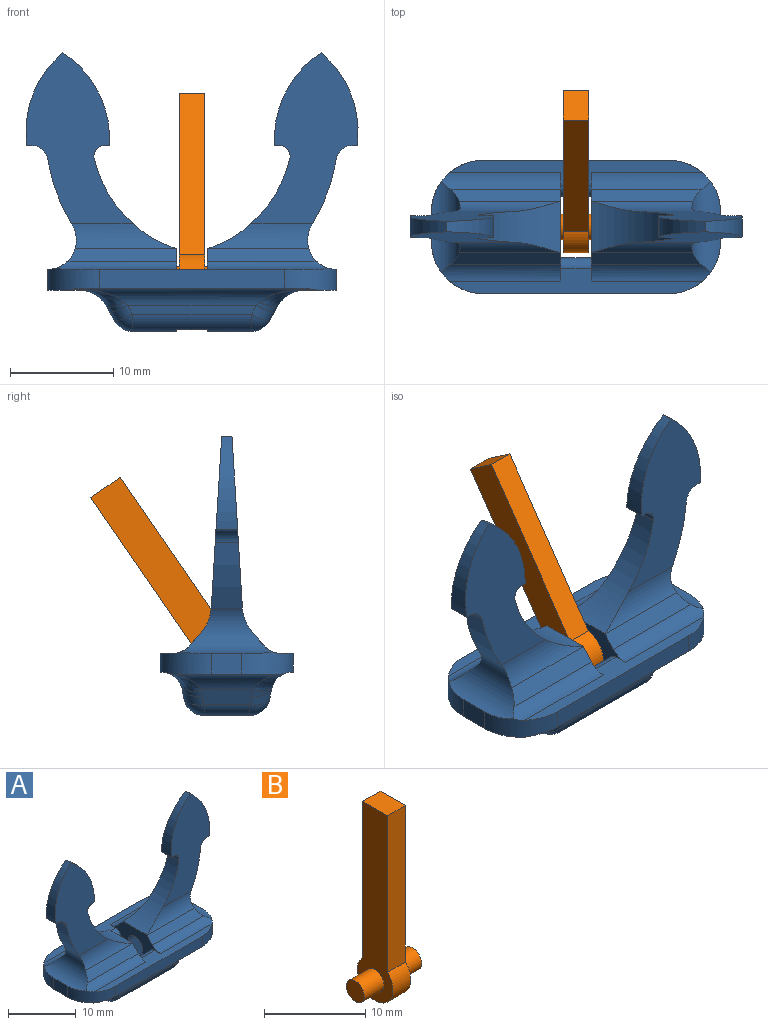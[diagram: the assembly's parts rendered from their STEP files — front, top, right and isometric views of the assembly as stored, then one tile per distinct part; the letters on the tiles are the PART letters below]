
ASSEMBLY  parts=2 mates=1
PART A: 96 faces, bbox 32.3x13x27.1 mm
  f0: plane 4.41x4.26mm, normal (0,0,-1), area 9.8mm2, adj f2,f10,f60,f61,f62,f75,f90
  f1: plane 10.48x8mm, normal (-1,0,0), area 31.6mm2, adj f3,f4,f24,f25,f35,f36,f50,f52
  f2: plane 10.48x8mm, normal (1,0,0), area 31.6mm2, adj f0,f4,f25,f26,f44,f45,f51,f53
  f3: plane 4.41x4.26mm, normal (0,0,-1), area 9.8mm2, adj f1,f11,f63,f64,f65,f75,f90
  f4: plane 24.54x2.46mm, normal (0,0,1), area 31.1mm2, adj f1,f2,f36,f38,f45,f68,f69,f82
  f5: cylinder r=2.8mm len=8.8mm, axis (0,1,0), area 33.5mm2, adj f6,f33,f43,f44,f45,f51,f53,f57
  f6: plane 2.91x2mm, normal (-1,0,0), area 5.8mm2, adj f5,f7,f66,f68
  f7: plane 10.31x3.07mm, normal (0,0,-1), area 28mm2, adj f6,f8,f66,f68,f80,f85
  f8: cylinder r=3mm len=10.31mm, axis (0,1,0), area 24.5mm2, adj f7,f9,f79,f86
  f9: plane 5.01x1.44mm, normal (-0.87,0,-0.49), area 7.7mm2, adj f8,f10,f77,f78,f87,f88
  f10: cylinder r=2mm len=4.41mm, axis (0,1,0), area 9.4mm2, adj f0,f9,f76,f89
  f11: cylinder r=2mm len=4.41mm, axis (0,1,0), area 9.4mm2, adj f3,f12,f74,f91
  f12: plane 5.01x1.44mm, normal (0.87,0,-0.49), area 7.7mm2, adj f11,f13,f72,f73,f92,f93
  f13: cylinder r=3mm len=10.31mm, axis (0,1,0), area 24.5mm2, adj f12,f14,f71,f94
  f14: plane 10.31x3.07mm, normal (0,0,-1), area 28mm2, adj f13,f15,f67,f69,f70,f95
  f15: plane 2.91x2mm, normal (1,0,0), area 5.8mm2, adj f14,f16,f67,f69
  f16: cylinder r=2.8mm len=8.8mm, axis (0,1,0), area 33.5mm2, adj f15,f17,f35,f36,f37,f50,f52,f56
  f17: cylinder r=18mm len=6.46mm, axis (0,1,0), area 18.3mm2, adj f16,f18,f34,f37,f54,f56
  f18: cylinder r=1.53mm len=2.25mm, axis (0,1,0), area 4.7mm2, adj f17,f19,f34,f54
  f19: plane 2.09x0.5mm, normal (0,0,-1), area 1mm2, adj f18,f20,f34,f54
  f20: cylinder r=10mm len=9mm, axis (0,1,0), area 15.6mm2, adj f19,f21,f34,f54
  f21: cylinder r=10mm len=9mm, axis (0,1,0), area 16.3mm2, adj f20,f22,f34,f54
  f22: plane 2.09x0.5mm, normal (0,0,-1), area 1mm2, adj f21,f23,f34,f54
  f23: cylinder r=1mm len=2.24mm, axis (0,1,0), area 3.9mm2, adj f22,f24,f34,f54
  f24: cylinder r=12mm len=8.78mm, axis (0,1,0), area 39.4mm2, adj f1,f23,f34,f37,f54,f56
  f25: plane 24.54x2.46mm, normal (0,0,1), area 31.1mm2, adj f1,f2,f49,f50,f51,f66,f67,f81
  f26: cylinder r=12mm len=8.78mm, axis (0,1,0), area 39.4mm2, adj f2,f27,f42,f43,f55,f57
  f27: cylinder r=1mm len=2.24mm, axis (0,1,0), area 3.9mm2, adj f26,f28,f42,f55
  f28: plane 2.09x0.5mm, normal (0,0,-1), area 1mm2, adj f27,f29,f42,f55
  f29: cylinder r=10mm len=9mm, axis (0,1,0), area 16.3mm2, adj f28,f30,f42,f55
  f30: cylinder r=10mm len=9mm, axis (0,1,0), area 15.6mm2, adj f29,f31,f42,f55
  f31: plane 2.09x0.5mm, normal (0,0,-1), area 1mm2, adj f30,f32,f42,f55
  f32: cylinder r=1.53mm len=2.25mm, axis (0,1,0), area 4.7mm2, adj f31,f33,f42,f55
  f33: cylinder r=18mm len=6.46mm, axis (0,1,0), area 18.3mm2, adj f5,f32,f42,f43,f55,f57
  f34: plane 16.68x10.47mm, normal (0,1,0.06), area 91.8mm2, adj f17,f18,f19,f20,f21,f22,f23,f24
  f35: plane 10.71x1.36mm, normal (0,0.75,0.66), area 17.1mm2, adj f1,f16,f36,f37
  f36: cylinder r=2.16mm len=11.54mm, axis (-1,0,0), area 20.4mm2, adj f1,f4,f16,f35,f69
  f37: cylinder r=4mm len=10.2mm, axis (-1,0,0), area 19.8mm2, adj f16,f17,f24,f34,f35
  f38: plane 18x1.83mm, normal (0,1,0), area 33mm2, adj f4,f39,f68,f69
  f39: plane 20.5x0.16mm, normal (0,0,-1), area 3.1mm2, adj f38,f40,f68,f69
  f40: cylinder r=2mm len=23.21mm, axis (-1,0,0), area 47.7mm2, adj f39,f41,f68,f69,f85,f86,f87,f93
  f41: plane 12.48x0.86mm, normal (0,0.98,-0.17), area 10.5mm2, adj f40,f88,f90,f92
  f42: plane 16.68x10.47mm, normal (0,1,0.06), area 91.8mm2, adj f26,f27,f28,f29,f30,f31,f32,f33
  f43: cylinder r=4mm len=10.2mm, axis (-1,0,0), area 19.8mm2, adj f5,f26,f33,f42,f44
  f44: plane 10.71x1.36mm, normal (0,0.75,0.66), area 17.1mm2, adj f2,f5,f43,f45
  f45: cylinder r=2.16mm len=11.54mm, axis (-1,0,0), area 20.4mm2, adj f2,f4,f5,f44,f68
  f46: plane 12.48x0.86mm, normal (0,-0.98,-0.17), area 10.5mm2, adj f48,f73,f75,f77
  f47: plane 20.5x0.16mm, normal (0,0,-1), area 3.1mm2, adj f48,f49,f66,f67
  f48: cylinder r=2mm len=23.21mm, axis (-1,0,0), area 47.7mm2, adj f46,f47,f66,f67,f70,f71,f72,f78
  f49: plane 18x1.83mm, normal (0,-1,0), area 33mm2, adj f25,f47,f66,f67
  f50: cylinder r=2.16mm len=11.54mm, axis (-1,0,0), area 20.4mm2, adj f1,f16,f25,f52,f67
  f51: cylinder r=2.16mm len=11.54mm, axis (-1,0,0), area 20.4mm2, adj f2,f5,f25,f53,f66
  f52: plane 10.71x1.36mm, normal (0,-0.75,0.66), area 17.1mm2, adj f1,f16,f50,f56
  f53: plane 10.71x1.36mm, normal (0,-0.75,0.66), area 17.1mm2, adj f2,f5,f51,f57
  f54: plane 16.68x10.47mm, normal (0,-1,0.06), area 91.8mm2, adj f17,f18,f19,f20,f21,f22,f23,f24
  f55: plane 16.68x10.47mm, normal (0,-1,0.06), area 91.8mm2, adj f26,f27,f28,f29,f30,f31,f32,f33
  f56: cylinder r=4mm len=10.2mm, axis (-1,0,0), area 19.8mm2, adj f16,f17,f24,f52,f54
  f57: cylinder r=4mm len=10.2mm, axis (-1,0,0), area 19.8mm2, adj f5,f26,f33,f53,f55
  f58: plane 4.84x3mm, normal (0,1,0), area 14.5mm2, adj f1,f2,f75,f81
  f59: plane 4.84x3mm, normal (0,-1,0), area 14.5mm2, adj f1,f2,f82,f90
  f60: plane 6.5x3mm, normal (1,0,0), area 18.5mm2, adj f0,f61,f62,f83
  f61: plane 5x3mm, normal (0,1,0), area 15mm2, adj f0,f2,f60,f83
  f62: plane 5x3mm, normal (0,-1,0), area 15mm2, adj f0,f2,f60,f83
  f63: plane 5x3mm, normal (0,-1,0), area 15mm2, adj f1,f3,f64,f84
  f64: plane 6.5x3mm, normal (-1,0,0), area 18.5mm2, adj f3,f63,f65,f84
  f65: plane 5x3mm, normal (0,1,0), area 15mm2, adj f1,f3,f64,f84
  f66: cylinder r=5mm len=5mm, axis (0,0,1), area 15.6mm2, adj f5,f6,f7,f25,f47,f48,f49,f51
  f67: cylinder r=5mm len=5mm, axis (0,0,-1), area 15.6mm2, adj f14,f15,f16,f25,f47,f48,f49,f50
  f68: cylinder r=5mm len=5mm, axis (0,0,-1), area 15.6mm2, adj f4,f5,f6,f7,f38,f39,f40,f45
  f69: cylinder r=5mm len=5mm, axis (0,0,1), area 15.6mm2, adj f4,f14,f15,f16,f36,f38,f39,f40
  f70: cylinder r=2mm len=1.44mm, axis (-1,0,0), area 0.6mm2, adj f14,f48,f67,f71
  f71: bspline ~4.69x3.31mm, area 6.7mm2, adj f13,f48,f70,f72
  f72: bspline ~2.07x2.04mm, area 1.5mm2, adj f12,f48,f71,f73
  f73: cylinder r=2mm len=2.23mm, axis (-0.48,0.15,-0.86), area 3mm2, adj f12,f46,f72,f74
  f74: sphere r=2mm, area 3.7mm2, adj f11,f73,f75
  f75: cylinder r=2mm len=11.52mm, axis (-1,0,0), area 29.7mm2, adj f0,f1,f2,f3,f46,f58,f74,f76
  f76: sphere r=2mm, area 3.7mm2, adj f10,f75,f77
  f77: cylinder r=2mm len=2.23mm, axis (-0.48,-0.15,0.86), area 3mm2, adj f9,f46,f76,f78
  f78: bspline ~2.07x2.04mm, area 1.5mm2, adj f9,f48,f77,f79
  f79: bspline ~5.07x3.39mm, area 6.7mm2, adj f8,f48,f78,f80
  f80: cylinder r=2mm len=1.44mm, axis (-1,0,0), area 0.6mm2, adj f7,f48,f66,f79
  f81: cylinder r=1mm len=3mm, axis (-1,0,0), area 4.7mm2, adj f1,f2,f25,f58
  f82: cylinder r=1mm len=3mm, axis (1,0,0), area 4.7mm2, adj f1,f2,f4,f59
  f83: cylinder r=1.5mm len=3mm, axis (1,0,0), area 14.1mm2, adj f2,f60,f61,f62
  f84: cylinder r=1.5mm len=3mm, axis (1,0,0), area 14.1mm2, adj f1,f63,f64,f65
  f85: cylinder r=2mm len=1.44mm, axis (-1,0,0), area 0.6mm2, adj f7,f40,f68,f86
  f86: bspline ~4.69x3.31mm, area 6.7mm2, adj f8,f40,f85,f87
  f87: bspline ~2.07x2.04mm, area 1.5mm2, adj f9,f40,f86,f88
  f88: cylinder r=2mm len=2.23mm, axis (0.48,-0.15,-0.86), area 3mm2, adj f9,f41,f87,f89
  f89: sphere r=2mm, area 3.7mm2, adj f10,f88,f90
  f90: cylinder r=2mm len=11.52mm, axis (1,0,0), area 29.7mm2, adj f0,f1,f2,f3,f41,f59,f89,f91
  f91: sphere r=2mm, area 3.7mm2, adj f11,f90,f92
  f92: cylinder r=2mm len=2.23mm, axis (0.48,0.15,0.86), area 3mm2, adj f12,f41,f91,f93
  f93: bspline ~2.07x2.04mm, area 1.5mm2, adj f12,f40,f92,f94
  f94: bspline ~5.07x3.39mm, area 6.7mm2, adj f13,f40,f93,f95
  f95: cylinder r=2mm len=1.44mm, axis (-1,0,0), area 0.6mm2, adj f14,f40,f69,f94
PART B: 10 faces, bbox 8x5x23.2 mm
  f0: plane 18.95x2.5mm, normal (0,-1,0), area 47.4mm2, adj f1,f3,f4,f5
  f1: cylinder r=2.5mm len=5mm, axis (-1,0,0), area 29.6mm2, adj f0,f2,f4,f5
  f2: plane 18.95x2.5mm, normal (0,1,0), area 47.4mm2, adj f1,f3,f4,f5
  f3: plane 3.5x2.5mm, normal (0,0,1), area 8.8mm2, adj f0,f2,f4,f5
  f4: plane 23.24x5mm, normal (1,0,0), area 79.3mm2, adj f0,f1,f2,f3,f8
  f5: plane 23.24x5mm, normal (-1,0,0), area 79.3mm2, adj f0,f1,f2,f3,f7
  f6: plane 2.5x2.5mm, normal (-1,0,0), area 4.9mm2, adj f7
  f7: cylinder r=1.25mm len=2.75mm, axis (-1,0,0), area 21.6mm2, adj f5,f6
  f8: cylinder r=1.25mm len=2.75mm, axis (-1,0,0), area 21.6mm2, adj f4,f9
  f9: plane 2.5x2.5mm, normal (1,0,0), area 4.9mm2, adj f8
PLACE A t=(-0.85,2.63,-3.39)mm fixed
PLACE B rot(axis=(-1,0,0),34.6deg) t=(-0.85,2.63,-3.39)mm
MATE revolute B.f7 <-> A.f83  axis (-1,0,0) through (-0.85,2.63,-3.39)mm
